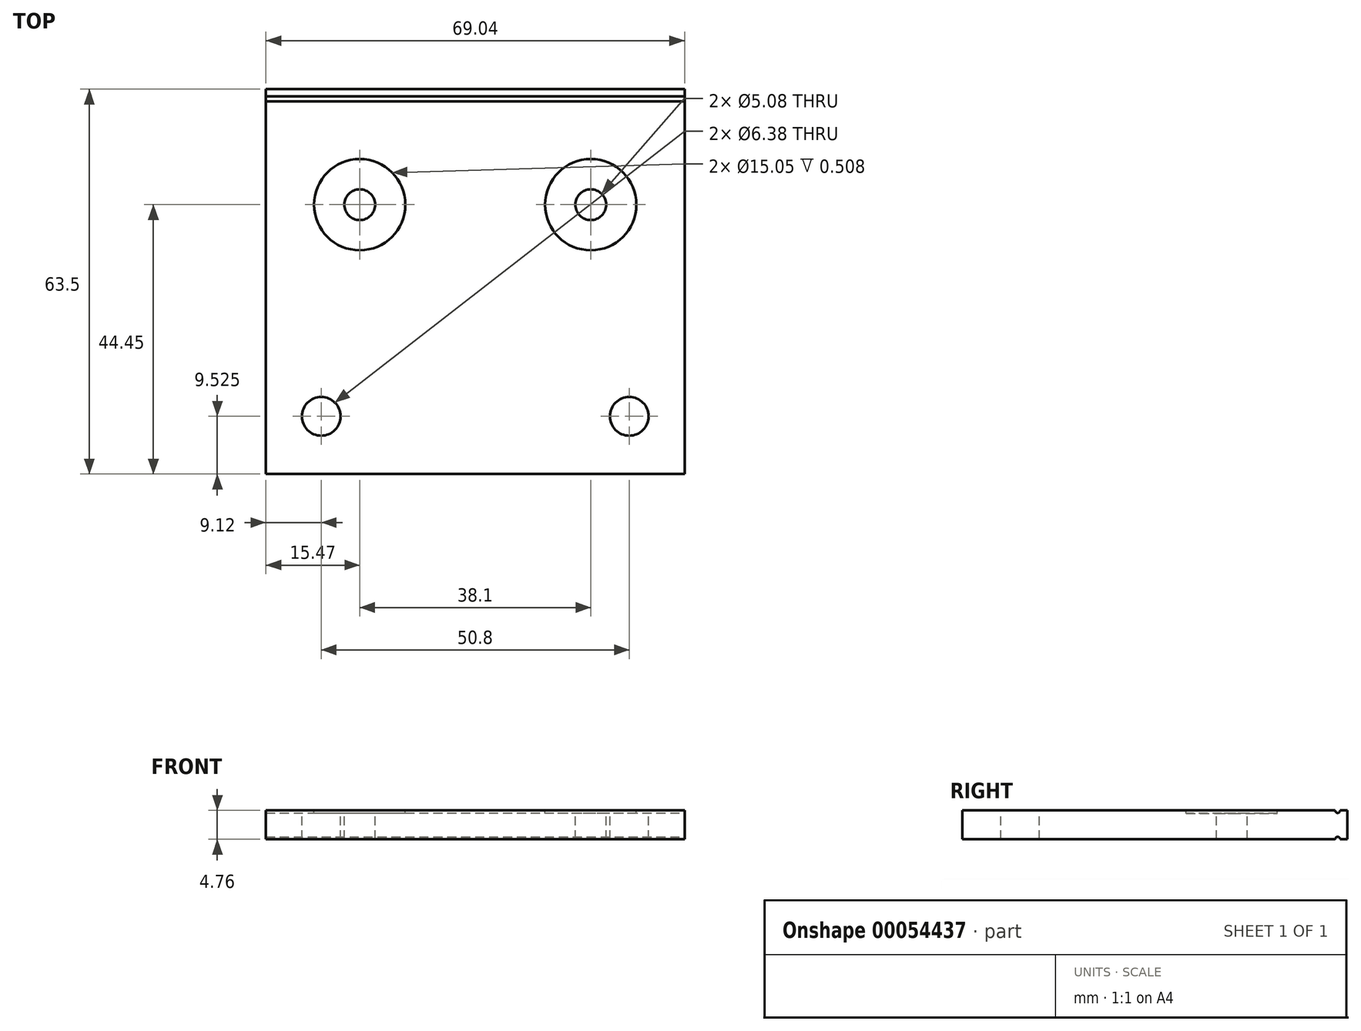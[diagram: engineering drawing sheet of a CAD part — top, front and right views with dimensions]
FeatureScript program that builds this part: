
annotation { "Feature Type Name" : "Feature", "Feature Type Description" : "" }
export const myFeature = defineFeature(function(context is Context, id is Id, definition is map)
    precondition{}
    {
        {
            var Q0;
            Q0=qCreatedBy(makeId("Top.planeOp"),FACE);
            var sketch = newSketch(context, id + "F0", { "sketchPlane" : qUnion([Q0])});
            skLineSegment(sketch, "E0.bottom", {"start": v(-34.52, 0) * mm, "end": v(34.52, 0) * mm});
            skLineSegment(sketch, "E0.top", {"start": v(-34.52, -63.5) * mm, "end": v(34.52, -63.5) * mm});
            skLineSegment(sketch, "E0.left", {"start": v(-34.52, 0) * mm, "end": v(-34.52, -63.5) * mm});
            skLineSegment(sketch, "E0.right", {"start": v(34.52, 0) * mm, "end": v(34.52, -63.5) * mm});
            skSolve(sketch);
        }
        {
            var Q0;
            Q0=makeQuery(id+"F0.imprint","IMPRINT",FACE,{"disambiguationData":[TD([[makeQuery(id+"F0.imprint","IMPRINT",EDGE,{"derivedFrom":sQuery(id+"F0.wireOp",EDGE,"E0.bottom")}),-1.0]])]});
            extrude(context, id + "F1", {"entities" : qUnion([Q0]), "depth" : 4.76 * mm, "offsetDistance" : 25.4 * mm});
        }
        {
            var Q0;
            Q0=makeQuery(id+"F1.opExtrude","CAP_FACE",FACE,{"disambiguationData":[OSD([sQuery(id+"F0.wireOp",EDGE,"E0.bottom"),sQuery(id+"F0.wireOp",EDGE,"E0.top"),sQuery(id+"F0.wireOp",EDGE,"E0.left"),sQuery(id+"F0.wireOp",EDGE,"E0.right")])],"isStart":false});
            var sketch = newSketch(context, id + "F2", { "sketchPlane" : qUnion([Q0])});
            skCircle(sketch, "E1", {"center": v(-25.4, -53.98) * mm, "radius": 3.19 * mm});
            skCircle(sketch, "E2", {"center": v(25.4, -53.98) * mm, "radius": 3.19 * mm});
            skSolve(sketch);
        }
        {
            var Q0;
            Q0=makeQuery(id+"F2.imprint","IMPRINT",FACE,{"disambiguationData":[TD([[makeQuery(id+"F2.imprint","IMPRINT",EDGE,{"derivedFrom":sQuery(id+"F2.wireOp",EDGE,"E2")}),1.0]])]});
            var Q1;
            Q1=makeQuery(id+"F2.imprint","IMPRINT",FACE,{"disambiguationData":[TD([[makeQuery(id+"F2.imprint","IMPRINT",EDGE,{"derivedFrom":sQuery(id+"F2.wireOp",EDGE,"E1")}),1.0]])]});
            var Q2;
            Q2=sQuery(id+"F2.wireOp",EDGE,"E1");
            var Q3;
            Q3=sQuery(id+"F2.wireOp",EDGE,"E2");
            extrude(context, id + "F3", {"entities" : qUnion([Q0, Q1]), "operationType" : NewBodyOperationType.REMOVE, "surfaceEntities" : qUnion([Q2, Q3]), "endBound" : BoundingType.THROUGH_ALL, "oppositeDirection" : true, "depth" : 25.4 * mm, "offsetDistance" : 25.4 * mm});
        }
        {
            var Q0;
            Q0=makeQuery(id+"F1.opExtrude","CAP_FACE",FACE,{"disambiguationData":[OSD([sQuery(id+"F0.wireOp",EDGE,"E0.bottom"),sQuery(id+"F0.wireOp",EDGE,"E0.top"),sQuery(id+"F0.wireOp",EDGE,"E0.left"),sQuery(id+"F0.wireOp",EDGE,"E0.right")])],"isStart":false});
            var sketch = newSketch(context, id + "F4", { "sketchPlane" : qUnion([Q0])});
            skCircle(sketch, "E3", {"center": v(-19.05, -19.05) * mm, "radius": 7.53 * mm});
            skCircle(sketch, "E4", {"center": v(19.05, -19.05) * mm, "radius": 7.53 * mm});
            skCircle(sketch, "E5", {"center": v(-19.05, -19.05) * mm, "radius": 2.54 * mm});
            skCircle(sketch, "E6", {"center": v(19.05, -19.05) * mm, "radius": 2.54 * mm});
            skSolve(sketch);
        }
        {
            var Q0;
            Q0=makeQuery(id+"F4.imprint","IMPRINT",FACE,{"disambiguationData":[TD([[makeQuery(id+"F4.imprint","IMPRINT",EDGE,{"derivedFrom":sQuery(id+"F4.wireOp",EDGE,"E5")}),1.0]])]});
            var Q1;
            Q1=makeQuery(id+"F4.imprint","IMPRINT",FACE,{"disambiguationData":[TD([[makeQuery(id+"F4.imprint","IMPRINT",EDGE,{"derivedFrom":sQuery(id+"F4.wireOp",EDGE,"E6")}),1.0]])]});
            extrude(context, id + "F5", {"entities" : qUnion([Q0, Q1]), "operationType" : NewBodyOperationType.REMOVE, "endBound" : BoundingType.THROUGH_ALL, "oppositeDirection" : true, "depth" : 25.4 * mm, "offsetDistance" : 25.4 * mm});
        }
        {
            var Q0;
            Q0 = qSketchRegion(id + "F4", true);
            extrude(context, id + "F6", {"entities" : qUnion([Q0]), "operationType" : NewBodyOperationType.REMOVE, "oppositeDirection" : true, "depth" : 0.5 * mm, "offsetDistance" : 25.4 * mm});
        }
        {
            var Q0;
            Q0=makeQuery(id+"F1.opExtrude","SWEPT_FACE",FACE,{"disambiguationData":[OSD([sQuery(id+"F0.wireOp",EDGE,"E0.right")])]});
            var sketch = newSketch(context, id + "F7", { "sketchPlane" : qUnion([Q0])});
            skCircle(sketch, "E7", {"center": v(-1.59, 4.76) * mm, "radius": 0.4 * mm});
            skCircle(sketch, "E8", {"center": v(-1.59, 0) * mm, "radius": 0.4 * mm});
            skSolve(sketch);
        }
        {
            var Q0;
            {var subQ0=sQuery(id+"F7.wireOp",EDGE,"E7");var subQ1=makeQuery(id+"F1.opExtrude","CAP_EDGE",EDGE,{"disambiguationData":[OSD([sQuery(id+"F0.wireOp",EDGE,"E0.right")])],"isStart":false});var subQ2=makeQuery(id+"F7.imprint","INTERSECT",VERTEX,{"disambiguationData":[OD(0.0)],"derivedFrom":[subQ1,subQ0]});Q0=makeQuery(id+"F7.imprint","IMPRINT",FACE,{"disambiguationData":[TD([[makeQuery(id+"F7.imprint","IMPRINT",EDGE,{"disambiguationData":[TD([[subQ2,1.0]])],"derivedFrom":subQ0}),1.0]])]});}
            var Q1;
            {var subQ0=sQuery(id+"F7.wireOp",EDGE,"E8");var subQ1=makeQuery(id+"F1.opExtrude","CAP_EDGE",EDGE,{"disambiguationData":[OSD([sQuery(id+"F0.wireOp",EDGE,"E0.right")])],"isStart":true});var subQ2=makeQuery(id+"F7.imprint","INTERSECT",VERTEX,{"disambiguationData":[OD(0.0)],"derivedFrom":[subQ1,subQ0]});Q1=makeQuery(id+"F7.imprint","IMPRINT",FACE,{"disambiguationData":[TD([[makeQuery(id+"F7.imprint","IMPRINT",EDGE,{"disambiguationData":[TD([[subQ2,-1.0]])],"derivedFrom":subQ0}),1.0]])]});}
            extrude(context, id + "F8", {"entities" : qUnion([Q0, Q1]), "operationType" : NewBodyOperationType.REMOVE, "endBound" : BoundingType.THROUGH_ALL, "oppositeDirection" : true, "depth" : 25.4 * mm, "offsetDistance" : 25.4 * mm});
        }
    });
